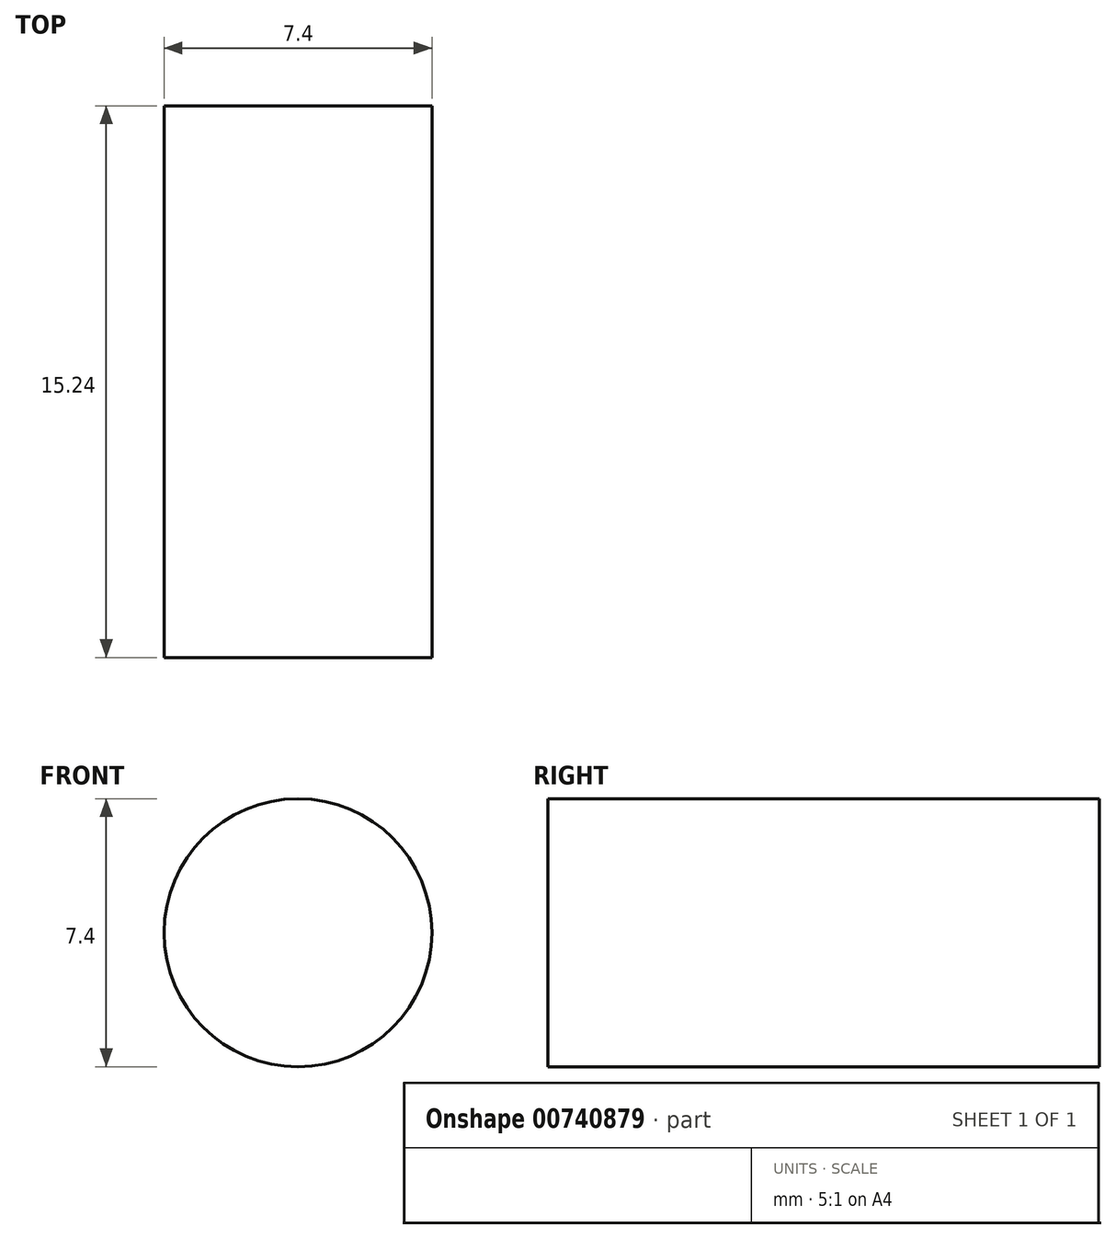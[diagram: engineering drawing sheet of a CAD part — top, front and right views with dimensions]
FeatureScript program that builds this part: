
annotation { "Feature Type Name" : "Feature", "Feature Type Description" : "" }
export const myFeature = defineFeature(function(context is Context, id is Id, definition is map)
    precondition{}
    {
        {
            var Q0;
            Q0=qCreatedBy(makeId("Front.planeOp"),FACE);
            var sketch = newSketch(context, id + "F0", { "sketchPlane" : qUnion([Q0])});
            skCircle(sketch, "E0", {"center": v(0, 0) * mm, "radius": 3.7 * mm});
            skSolve(sketch);
        }
        {
            var Q0;
            Q0 = qSketchRegion(id + "F0", true);
            extrude(context, id + "F1", {"entities" : qUnion([Q0]), "depth" : 15.24 * mm, "offsetDistance" : 25.4 * mm});
        }
    });
